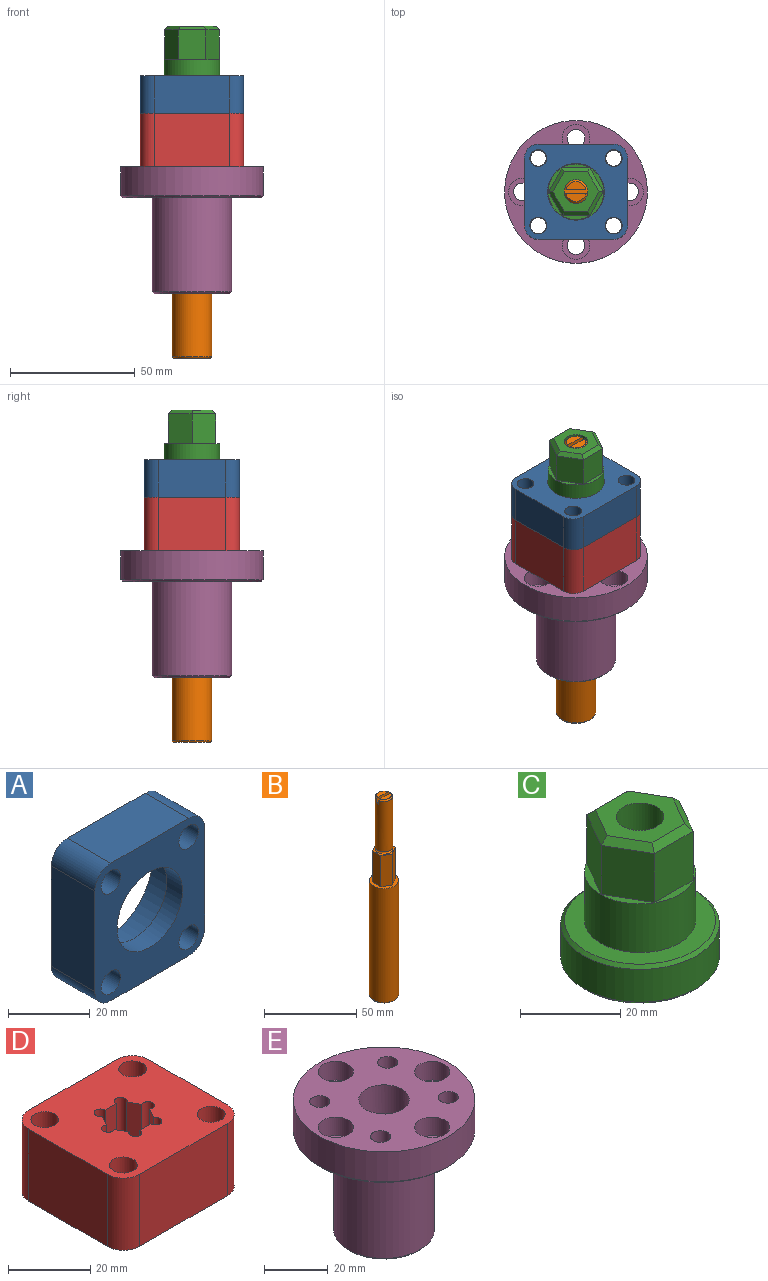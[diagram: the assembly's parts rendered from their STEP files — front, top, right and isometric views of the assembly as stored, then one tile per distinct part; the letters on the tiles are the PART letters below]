
ASSEMBLY  parts=5 mates=4
PART A: 18 faces, bbox 38.1x15.1x41.3 mm
  f0: plane 30.15x15.09mm, normal (-1,0,0), area 454.9mm2, adj f4,f5,f9,f10
  f1: plane 26.97x15.09mm, normal (0,0,-1), area 407mm2, adj f4,f5,f10,f11
  f2: plane 30.15x15.09mm, normal (1,0,0), area 454.9mm2, adj f4,f5,f11,f12
  f3: plane 26.97x15.09mm, normal (0,0,1), area 407mm2, adj f4,f5,f9,f12
  f4: plane 41.28x38.1mm, normal (0,-1,0), area 997.1mm2, adj f0,f1,f2,f3,f8,f9,f10,f11
  f5: plane 41.28x38.1mm, normal (0,1,0), area 585.7mm2, adj f0,f1,f2,f3,f6,f9,f10,f11
  f6: cylinder r=16.13mm len=32.26mm, axis (0,1,0), area 926.7mm2, adj f5,f17
  f7: plane 31.24x31.24mm, normal (0,1,0), area 360.7mm2, adj f8,f17
  f8: cylinder r=11.37mm len=22.73mm, axis (0,-1,0), area 388.2mm2, adj f4,f7
  f9: cylinder r=5.56mm len=15.09mm, axis (0,1,0), area 131.8mm2, adj f0,f3,f4,f5
  f10: cylinder r=5.56mm len=15.09mm, axis (0,1,0), area 131.8mm2, adj f0,f1,f4,f5
  f11: cylinder r=5.56mm len=15.09mm, axis (0,1,0), area 131.8mm2, adj f1,f2,f4,f5
  f12: cylinder r=5.56mm len=15.09mm, axis (0,1,0), area 131.8mm2, adj f2,f3,f4,f5
  f13: cylinder r=3.37mm len=15.09mm, axis (0,-1,0), area 319.8mm2, adj f4,f5
  f14: cylinder r=3.37mm len=15.09mm, axis (0,-1,0), area 319.8mm2, adj f4,f5
  f15: cylinder r=3.37mm len=15.09mm, axis (0,-1,0), area 319.8mm2, adj f4,f5
  f16: cylinder r=3.37mm len=15.09mm, axis (0,-1,0), area 319.8mm2, adj f4,f5
  f17: torus R=15.62mm, axis (0,1,0), area 79.9mm2, adj f6,f7
PART B: 20 faces, bbox 17.1x17.1x132.6 mm
  f0: cylinder r=7.91mm len=75.69mm, axis (0,0,-1), area 3762.9mm2, adj f1,f19
  f1: plane 15.82x15.82mm, normal (0,0,1), area 89.7mm2, adj f0,f3,f4,f5,f6,f7,f8
  f2: plane 14.81x14.81mm, normal (0,0,-1), area 172.2mm2, adj f19
  f3: plane 20.64x5.56mm, normal (0.5,0.87,0), area 132.4mm2, adj f1,f4,f8,f9
  f4: plane 20.64x5.56mm, normal (-0.5,0.87,0), area 132.4mm2, adj f1,f3,f5,f9
  f5: plane 20.64x6.42mm, normal (-1,0,0), area 132.4mm2, adj f1,f4,f6,f9
  f6: plane 20.64x5.56mm, normal (-0.5,-0.87,0), area 132.4mm2, adj f1,f5,f7,f9
  f7: plane 20.64x5.56mm, normal (0.5,-0.87,0), area 132.4mm2, adj f1,f6,f8,f9
  f8: plane 20.64x6.42mm, normal (1,0,0), area 132.4mm2, adj f1,f3,f7,f9
  f9: plane 12.83x11.11mm, normal (0,0,1), area 35.7mm2, adj f3,f4,f5,f6,f7,f8,f10
  f10: torus R=4.76mm, axis (0,0,1), area 66.7mm2, adj f9,f18
  f11: plane 7.84x3.21mm, normal (0,0,1), area 18.8mm2, adj f13,f14
  f12: plane 7.84x3.21mm, normal (0,0,1), area 18.8mm2, adj f15,f16
  f13: cone r=4mm half-angle=45deg, axis (0,0,-1), area 13.1mm2, adj f11,f14,f18
  f14: plane 9.4x3.19mm, normal (0,-1,0), area 29.2mm2, adj f11,f13,f17,f18
  f15: cone r=4mm half-angle=45deg, axis (0,0,-1), area 13.1mm2, adj f12,f16,f18
  f16: plane 9.4x3.19mm, normal (0,1,0), area 29.2mm2, adj f12,f15,f17,f18
  f17: plane 9.53x1.59mm, normal (0,0,1), area 15.1mm2, adj f14,f16,f18
  f18: cylinder r=4.76mm len=33.37mm, axis (0,0,-1), area 990.8mm2, adj f10,f13,f14,f15,f16,f17
  f19: torus R=7.4mm, axis (0,0,1), area 38.7mm2, adj f0,f2
PART C: 23 faces, bbox 31.8x31.8x34.9 mm
  f0: cylinder r=15.88mm len=31.75mm, axis (0,0,-1), area 798.1mm2, adj f15,f16
  f1: plane 30.23x30.23mm, normal (0,0,1), area 329.6mm2, adj f3,f15
  f2: plane 30.23x30.23mm, normal (0,0,-1), area 633.9mm2, adj f13,f16
  f3: cylinder r=11.11mm len=22.23mm, axis (0,0,-1), area 831.3mm2, adj f1,f4
  f4: plane 22.23x22.23mm, normal (0,0,1), area 73.7mm2, adj f3,f5,f6,f7,f8,f9,f10
  f5: plane 11.97x11mm, normal (0,1,0), area 131.6mm2, adj f4,f6,f10,f22
  f6: plane 11.97x9.53mm, normal (-0.87,0.5,0), area 131.6mm2, adj f4,f5,f7,f21
  f7: plane 11.97x9.53mm, normal (-0.87,-0.5,0), area 131.6mm2, adj f4,f6,f8,f19
  f8: plane 11.97x11mm, normal (0,-1,0), area 131.6mm2, adj f4,f7,f9,f17
  f9: plane 11.97x9.53mm, normal (0.87,-0.5,0), area 131.6mm2, adj f4,f8,f10,f18
  f10: plane 11.97x9.53mm, normal (0.87,0.5,0), area 131.6mm2, adj f4,f5,f9,f20
  f11: plane 18.48x16mm, normal (0,0,1), area 150.5mm2, adj f14,f17,f18,f19,f20,f21,f22
  f12: cone r=5.16mm half-angle=59deg, axis (0,0,-1), area 14.4mm2, adj f13,f14
  f13: cylinder r=5.16mm len=10.32mm, axis (0,0,-1), area 257.3mm2, adj f2,f12
  f14: cylinder r=4.76mm len=26.75mm, axis (0,0,-1), area 800.4mm2, adj f11,f12
  f15: cone r=15.11mm half-angle=45deg, axis (0,0,-1), area 104.9mm2, adj f0,f1
  f16: cone r=15.88mm half-angle=45deg, axis (0,0,1), area 104.9mm2, adj f0,f2
  f17: plane 11x1.52mm, normal (0,-0.71,0.71), area 21.8mm2, adj f8,f11,f18,f19
  f18: plane 9.53x6.38mm, normal (0.61,-0.35,0.71), area 21.8mm2, adj f9,f11,f17,f20
  f19: plane 9.53x6.38mm, normal (-0.61,-0.35,0.71), area 21.8mm2, adj f7,f11,f17,f21
  f20: plane 9.53x6.38mm, normal (0.61,0.35,0.71), area 21.8mm2, adj f10,f11,f18,f22
  f21: plane 9.53x6.38mm, normal (-0.61,0.35,0.71), area 21.8mm2, adj f6,f11,f19,f22
  f22: plane 11x1.52mm, normal (0,0.71,0.71), area 21.8mm2, adj f5,f11,f20,f21
PART D: 26 faces, bbox 41.3x38.1x21.4 mm
  f0: plane 26.99x21.43mm, normal (1,0,0), area 578.4mm2, adj f4,f5,f23,f24
  f1: plane 30.16x21.43mm, normal (0,1,0), area 646.4mm2, adj f4,f5,f22,f23
  f2: plane 26.99x21.43mm, normal (-1,0,0), area 578.4mm2, adj f4,f5,f22,f25
  f3: plane 30.16x21.43mm, normal (0,-1,0), area 646.4mm2, adj f4,f5,f24,f25
  f4: plane 41.28x38.1mm, normal (0,0,1), area 1248.6mm2, adj f0,f1,f2,f3,f6,f7,f8,f9
  f5: plane 41.28x38.1mm, normal (0,0,-1), area 1248.6mm2, adj f0,f1,f2,f3,f6,f7,f8,f9
  f6: cylinder r=1.59mm len=21.43mm, axis (0,0,1), area 142.5mm2, adj f4,f5,f7,f17
  f7: plane 21.43x3.7mm, normal (0,-1,0), area 79.3mm2, adj f4,f5,f6,f8
  f8: cylinder r=1.59mm len=21.43mm, axis (0,0,1), area 142.5mm2, adj f4,f5,f7,f9
  f9: plane 21.43x3.2mm, normal (-0.87,-0.5,0), area 79.3mm2, adj f4,f5,f8,f10
  f10: cylinder r=1.59mm len=21.43mm, axis (0,0,1), area 142.5mm2, adj f4,f5,f9,f11
  f11: plane 21.43x3.2mm, normal (-0.87,0.5,0), area 79.3mm2, adj f4,f5,f10,f12
  f12: cylinder r=1.59mm len=21.43mm, axis (0,0,1), area 142.5mm2, adj f4,f5,f11,f13
  f13: plane 21.43x3.7mm, normal (0,1,0), area 79.3mm2, adj f4,f5,f12,f14
  f14: cylinder r=1.59mm len=21.43mm, axis (0,0,1), area 142.5mm2, adj f4,f5,f13,f15
  f15: plane 21.43x3.2mm, normal (0.87,0.5,0), area 79.3mm2, adj f4,f5,f14,f16
  f16: cylinder r=1.59mm len=21.43mm, axis (0,0,1), area 142.5mm2, adj f4,f5,f15,f17
  f17: plane 21.43x3.2mm, normal (0.87,-0.5,0), area 79.3mm2, adj f4,f5,f6,f16
  f18: cylinder r=3.37mm len=21.43mm, axis (0,0,1), area 454.3mm2, adj f4,f5
  f19: cylinder r=3.37mm len=21.43mm, axis (0,0,1), area 454.3mm2, adj f4,f5
  f20: cylinder r=3.37mm len=21.43mm, axis (0,0,1), area 454.3mm2, adj f4,f5
  f21: cylinder r=3.37mm len=21.43mm, axis (0,0,1), area 454.3mm2, adj f4,f5
  f22: cylinder r=5.56mm len=21.43mm, axis (0,0,-1), area 187mm2, adj f1,f2,f4,f5
  f23: cylinder r=5.56mm len=21.43mm, axis (0,0,-1), area 187mm2, adj f0,f1,f4,f5
  f24: cylinder r=5.56mm len=21.43mm, axis (0,0,-1), area 187mm2, adj f0,f3,f4,f5
  f25: cylinder r=5.56mm len=21.43mm, axis (0,0,-1), area 187mm2, adj f2,f3,f4,f5
PART E: 27 faces, bbox 57.2x57.2x50.8 mm
  f0: cylinder r=7.94mm len=47.8mm, axis (0,0,1), area 2384.1mm2, adj f4,f6
  f1: cylinder r=15.85mm len=37.74mm, axis (0,0,-1), area 3758.8mm2, adj f5,f10
  f2: plane 30.18x30.18mm, normal (0,0,-1), area 316.5mm2, adj f7,f10
  f3: cylinder r=28.57mm len=57.15mm, axis (0,0,-1), area 2070.4mm2, adj f4,f9
  f4: plane 57.15x57.15mm, normal (0,0,1), area 1852.6mm2, adj f0,f3,f13,f16,f19,f22,f23,f24
  f5: plane 55.63x55.63mm, normal (0,0,-1), area 1354mm2, adj f1,f9,f11,f14,f17,f20,f23,f24
  f6: plane 21.01x21.01mm, normal (0,0,-1), area 148.6mm2, adj f0,f8
  f7: cylinder r=11.26mm len=22.53mm, axis (0,0,-1), area 158.2mm2, adj f2,f8
  f8: torus R=10.5mm, axis (0,0,-1), area 82.6mm2, adj f6,f7
  f9: cone r=28.57mm half-angle=45deg, axis (0,0,1), area 190.9mm2, adj f3,f5
  f10: cone r=15.85mm half-angle=45deg, axis (0,0,1), area 104.7mm2, adj f1,f2
  f11: cylinder r=3.57mm len=7.14mm, axis (0,0,1), area 115.6mm2, adj f5,f12
  f12: plane 11.11x11.11mm, normal (0,0,1), area 56.9mm2, adj f11,f13
  f13: cylinder r=5.56mm len=11.11mm, axis (0,0,1), area 249.4mm2, adj f4,f12
  f14: cylinder r=3.57mm len=7.14mm, axis (0,0,1), area 115.6mm2, adj f5,f15
  f15: plane 11.11x11.11mm, normal (0,0,1), area 56.9mm2, adj f14,f16
  f16: cylinder r=5.56mm len=11.11mm, axis (0,0,1), area 249.4mm2, adj f4,f15
  f17: cylinder r=3.57mm len=7.14mm, axis (0,0,1), area 115.6mm2, adj f5,f18
  f18: plane 11.11x11.11mm, normal (0,0,1), area 56.9mm2, adj f17,f19
  f19: cylinder r=5.56mm len=11.11mm, axis (0,0,1), area 249.4mm2, adj f4,f18
  f20: cylinder r=3.57mm len=7.14mm, axis (0,0,1), area 115.6mm2, adj f5,f21
  f21: plane 11.11x11.11mm, normal (0,0,1), area 56.9mm2, adj f20,f22
  f22: cylinder r=5.56mm len=11.11mm, axis (0,0,1), area 249.4mm2, adj f4,f21
  f23: cylinder r=3.17mm len=12.29mm, axis (0,0,1), area 245.2mm2, adj f4,f5
  f24: cylinder r=3.17mm len=12.29mm, axis (0,0,1), area 245.2mm2, adj f4,f5
  f25: cylinder r=3.17mm len=12.29mm, axis (0,0,1), area 245.2mm2, adj f4,f5
  f26: cylinder r=3.17mm len=12.29mm, axis (0,0,1), area 245.2mm2, adj f4,f5
PLACE A rot(axis=(-0.58,-0.58,0.58),120deg) t=(0.01,-0.01,21.43)mm
PLACE B rot(axis=(0,0,1),180deg) t=(0,0,-76.5)mm
PLACE C rot(axis=(0,0,-1),179.6deg) t=(0,0,21.43)mm
PLACE D at identity
PLACE E t=(0,0,-50.8)mm
MATE revolute C.f13 <-> D.f4  axis (0,0,-1) through (0,0,21.43)mm
MATE cylindrical B.f13 <-> C.f13  axis (0,0,-1) through (0,0,38.61)mm
MATE fastened D.f21 <-> E.f26  axis (0,0,-1) through (15.08,-13.49,0)mm
MATE fastened A.f15 <-> D.f20  axis (0,0,-1) through (-15.08,-13.49,21.43)mm
